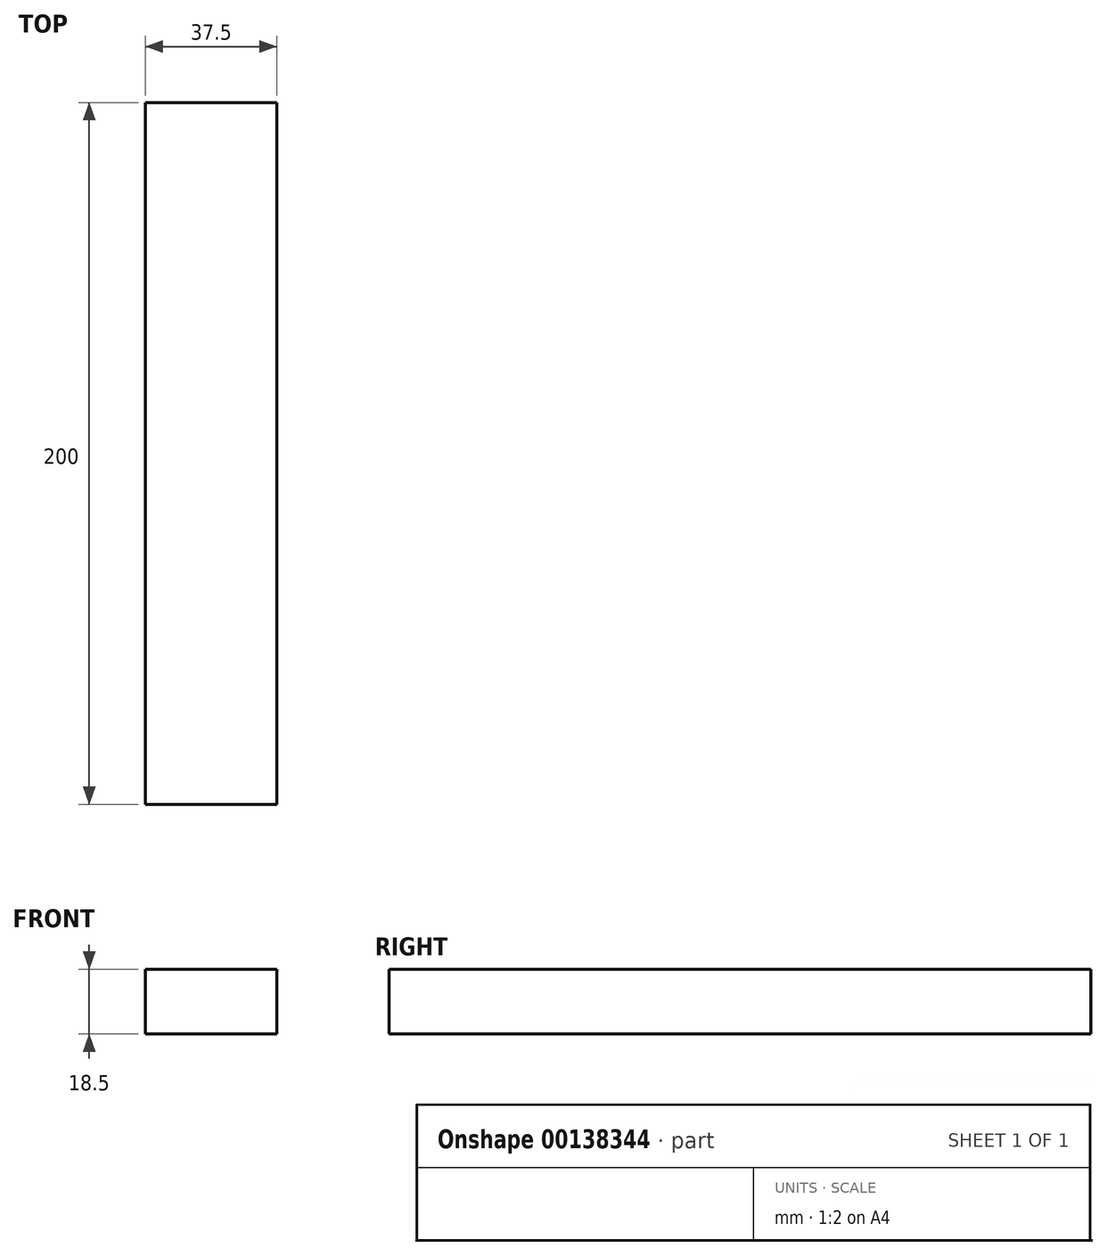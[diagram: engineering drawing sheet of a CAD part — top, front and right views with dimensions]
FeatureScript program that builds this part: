
annotation { "Feature Type Name" : "Feature", "Feature Type Description" : "" }
export const myFeature = defineFeature(function(context is Context, id is Id, definition is map)
    precondition{}
    {
        {
            var Q0;
            Q0=qCreatedBy(makeId("Front.planeOp"),FACE);
            var sketch = newSketch(context, id + "F0", { "sketchPlane" : qUnion([Q0])});
            skLineSegment(sketch, "E0.bottom", {"start": v(0, 0) * mm, "end": v(-37.5, 0) * mm});
            skLineSegment(sketch, "E0.top", {"start": v(0, -18.5) * mm, "end": v(-37.5, -18.5) * mm});
            skLineSegment(sketch, "E0.left", {"start": v(0, 0) * mm, "end": v(0, -18.5) * mm});
            skLineSegment(sketch, "E0.right", {"start": v(-37.5, 0) * mm, "end": v(-37.5, -18.5) * mm});
            skSolve(sketch);
        }
        {
            var Q0;
            Q0 = qSketchRegion(id + "F0", true);
            extrude(context, id + "F1", {"entities" : qUnion([Q0]), "depth" : 200 * mm});
        }
    });
